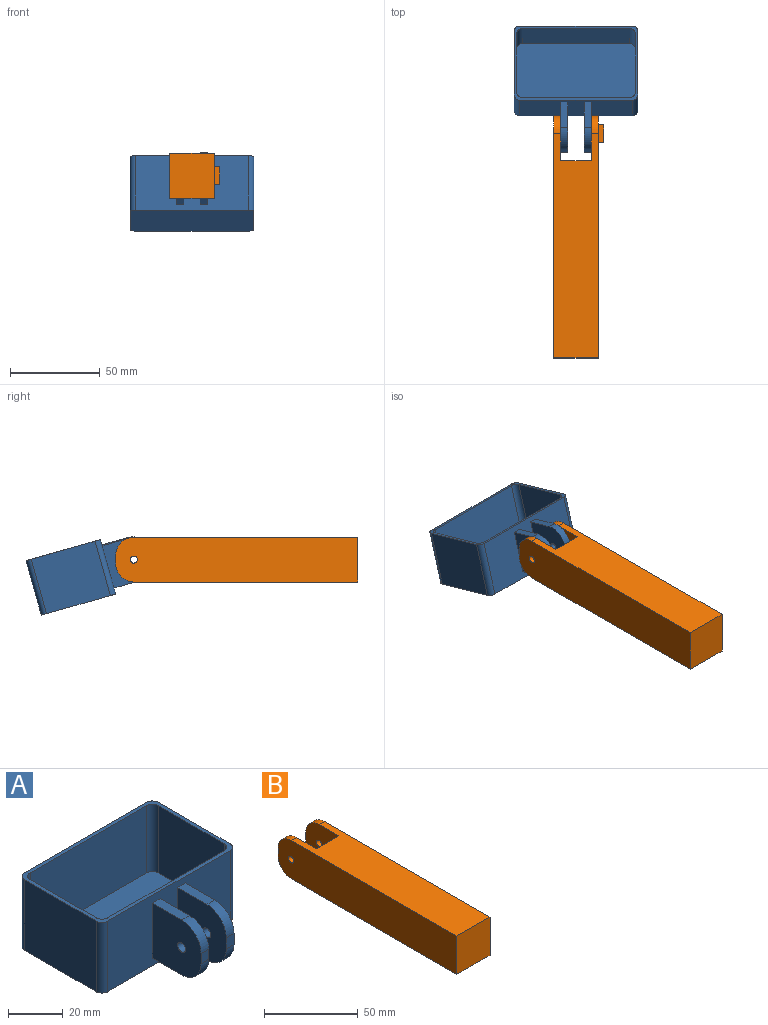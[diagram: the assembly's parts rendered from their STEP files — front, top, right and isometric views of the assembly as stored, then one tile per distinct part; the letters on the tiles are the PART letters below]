
ASSEMBLY  parts=2 mates=1
PART A: 35 faces, bbox 69x68x31.5 mm
  f0: plane 63x31.5mm, normal (0,-1,0), area 1786.5mm2, adj f4,f9,f15,f18,f19,f20,f21,f22
  f1: plane 37x31.5mm, normal (1,0,0), area 1165.5mm2, adj f4,f9,f15,f16
  f2: plane 63x31.5mm, normal (0,1,0), area 1984.5mm2, adj f4,f9,f16,f17
  f3: plane 37x31.5mm, normal (-1,0,0), area 1165.5mm2, adj f4,f9,f17,f18
  f4: plane 69x43mm, normal (0,0,-1), area 2959.3mm2, adj f0,f1,f2,f3,f15,f16,f17,f18
  f5: plane 60x30mm, normal (0,1,0), area 1800mm2, adj f9,f10,f11,f12
  f6: plane 34x30mm, normal (1,0,0), area 1020mm2, adj f9,f10,f11,f13
  f7: plane 60x30mm, normal (0,-1,0), area 1800mm2, adj f9,f10,f13,f14
  f8: plane 34x30mm, normal (-1,0,0), area 1020mm2, adj f9,f10,f12,f14
  f9: plane 69x43mm, normal (0,0,1), area 327mm2, adj f0,f1,f2,f3,f5,f6,f7,f8
  f10: plane 66x40mm, normal (0,0,1), area 2632.3mm2, adj f5,f6,f7,f8,f11,f12,f13,f14
  f11: cylinder r=3mm len=30mm, axis (0,0,1), area 141.4mm2, adj f5,f6,f9,f10
  f12: cylinder r=3mm len=30mm, axis (0,0,-1), area 141.4mm2, adj f5,f8,f9,f10
  f13: cylinder r=3mm len=30mm, axis (0,0,1), area 141.4mm2, adj f6,f7,f9,f10
  f14: cylinder r=3mm len=30mm, axis (0,0,-1), area 141.4mm2, adj f7,f8,f9,f10
  f15: cylinder r=3mm len=31.5mm, axis (0,0,1), area 148.4mm2, adj f0,f1,f4,f9
  f16: cylinder r=3mm len=31.5mm, axis (0,0,-1), area 148.4mm2, adj f1,f2,f4,f9
  f17: cylinder r=3mm len=31.5mm, axis (0,0,1), area 148.4mm2, adj f2,f3,f4,f9
  f18: cylinder r=3mm len=31.5mm, axis (0,0,-1), area 148.4mm2, adj f0,f3,f4,f9
  f19: plane 15x4mm, normal (0,0,1), area 60mm2, adj f0,f20,f22,f34
  f20: plane 25x24.5mm, normal (-1,0,0), area 557mm2, adj f0,f19,f21,f23,f30,f33,f34
  f21: plane 15x4mm, normal (0,0,-1), area 60mm2, adj f0,f20,f22,f33
  f22: plane 25x24.5mm, normal (1,0,0), area 557mm2, adj f0,f19,f21,f23,f30,f33,f34
  f23: plane 4.5x4mm, normal (0,-1,0), area 18mm2, adj f20,f22,f33,f34
  f24: plane 25x25mm, normal (1,0,0), area 569.5mm2, adj f0,f25,f27,f28,f29,f31,f32
  f25: plane 15x4mm, normal (0,0,1), area 60mm2, adj f0,f24,f26,f31
  f26: plane 25x25mm, normal (-1,0,0), area 569.5mm2, adj f0,f25,f27,f28,f29,f31,f32
  f27: plane 15x4mm, normal (0,0,-1), area 60mm2, adj f0,f24,f26,f32
  f28: plane 5x4mm, normal (0,-1,0), area 20mm2, adj f24,f26,f31,f32
  f29: cylinder r=2mm len=4mm, axis (-1,0,0), area 50.3mm2, adj f24,f26
  f30: cylinder r=2mm len=4mm, axis (-1,0,0), area 50.3mm2, adj f20,f22
  f31: cylinder r=10mm len=10mm, axis (1,0,0), area 62.8mm2, adj f24,f25,f26,f28
  f32: cylinder r=10mm len=10mm, axis (-1,0,0), area 62.8mm2, adj f24,f26,f27,f28
  f33: cylinder r=10mm len=10mm, axis (-1,0,0), area 62.8mm2, adj f20,f21,f22,f23
  f34: cylinder r=10mm len=10mm, axis (1,0,0), area 62.8mm2, adj f19,f20,f22,f23
PART B: 52 faces, bbox 28x135x25 mm
  f0: plane 25x17mm, normal (0,1,0), area 425mm2, adj f4,f5,f6,f8
  f1: plane 25x25mm, normal (0,-1,0), area 625mm2, adj f2,f3,f4,f5
  f2: plane 135x25mm, normal (1,0,0), area 3232.1mm2, adj f1,f4,f5,f7,f10,f11,f12,f13
  f3: plane 135x25mm, normal (-1,0,0), area 3319.5mm2, adj f1,f4,f5,f9,f22,f24,f25
  f4: plane 125x25mm, normal (0,0,-1), area 2870mm2, adj f0,f1,f2,f3,f6,f8,f24,f27
  f5: plane 125x25mm, normal (0,0,1), area 2870mm2, adj f0,f1,f2,f3,f6,f8,f25,f26
  f6: plane 25x25mm, normal (-1,0,0), area 569.5mm2, adj f0,f4,f5,f7,f23,f26,f27
  f7: plane 5x4mm, normal (0,1,0), area 20mm2, adj f2,f6,f26,f27
  f8: plane 25x25mm, normal (1,0,0), area 569.5mm2, adj f0,f4,f5,f9,f22,f24,f25
  f9: plane 5x4mm, normal (0,1,0), area 20mm2, adj f3,f8,f24,f25
  f10: plane 10x3mm, normal (0,0,-1), area 30mm2, adj f2,f11,f13,f14
  f11: plane 10x3mm, normal (0,1,0), area 30mm2, adj f2,f10,f12,f14
  f12: plane 10x3mm, normal (0,0,1), area 30mm2, adj f2,f11,f13,f14
  f13: plane 10x3mm, normal (0,-1,0), area 30mm2, adj f2,f10,f12,f14
  f14: plane 10x10mm, normal (1,0,0), area 57.6mm2, adj f10,f11,f12,f13,f15,f16,f17,f18
  f15: plane 3.5x3mm, normal (0,-0.5,0.87), area 12.1mm2, adj f14,f16,f20,f21
  f16: plane 4.04x3mm, normal (0,-1,0), area 12.1mm2, adj f14,f15,f17,f21
  f17: plane 3.5x3mm, normal (0,-0.5,-0.87), area 12.1mm2, adj f14,f16,f18,f21
  f18: plane 3.5x3mm, normal (0,0.5,-0.87), area 12.1mm2, adj f14,f17,f19,f21
  f19: plane 4.04x3mm, normal (0,1,0), area 12.1mm2, adj f14,f18,f20,f21
  f20: plane 3.5x3mm, normal (0,0.5,0.87), area 12.1mm2, adj f14,f15,f19,f21
  f21: plane 8.08x7mm, normal (1,0,0), area 29.9mm2, adj f15,f16,f17,f18,f19,f20,f23
  f22: cylinder r=2mm len=4mm, axis (1,0,0), area 50.3mm2, adj f3,f8
  f23: cylinder r=2mm len=4mm, axis (1,0,0), area 50.3mm2, adj f6,f21
  f24: cylinder r=10mm len=10mm, axis (1,0,0), area 62.8mm2, adj f3,f4,f8,f9
  f25: cylinder r=10mm len=10mm, axis (-1,0,0), area 62.8mm2, adj f3,f5,f8,f9
  f26: cylinder r=10mm len=10mm, axis (-1,0,0), area 62.8mm2, adj f2,f5,f6,f7
  f27: cylinder r=10mm len=10mm, axis (1,0,0), area 62.8mm2, adj f2,f4,f6,f7
  f28: plane 21x20mm, normal (0,0,-1), area 420mm2, adj f30,f31,f32,f33
  f29: plane 21x20mm, normal (0,0,1), area 420mm2, adj f30,f31,f32,f33
  f30: plane 21x20mm, normal (-1,0,0), area 420mm2, adj f28,f29,f31,f33
  f31: plane 21x21mm, normal (0,-1,0), area 441mm2, adj f28,f29,f30,f32
  f32: plane 21x20mm, normal (1,0,0), area 420mm2, adj f28,f29,f31,f33
  f33: plane 21x21mm, normal (0,1,0), area 441mm2, adj f28,f29,f30,f32
  f34: plane 21x20mm, normal (0,0,1), area 420mm2, adj f35,f36,f37,f38
  f35: plane 21x21mm, normal (0,1,0), area 441mm2, adj f34,f36,f38,f39
  f36: plane 21x20mm, normal (-1,0,0), area 420mm2, adj f34,f35,f37,f39
  f37: plane 21x21mm, normal (0,-1,0), area 441mm2, adj f34,f36,f38,f39
  f38: plane 21x20mm, normal (1,0,0), area 420mm2, adj f34,f35,f37,f39
  f39: plane 21x20mm, normal (0,0,-1), area 420mm2, adj f35,f36,f37,f38
  f40: plane 30x21mm, normal (0,0,1), area 630mm2, adj f41,f42,f43,f44
  f41: plane 21x21mm, normal (0,1,0), area 441mm2, adj f40,f42,f44,f45
  f42: plane 30x21mm, normal (-1,0,0), area 630mm2, adj f40,f41,f43,f45
  f43: plane 21x21mm, normal (0,-1,0), area 441mm2, adj f40,f42,f44,f45
  f44: plane 30x21mm, normal (1,0,0), area 630mm2, adj f40,f41,f43,f45
  f45: plane 30x21mm, normal (0,0,-1), area 630mm2, adj f41,f42,f43,f44
  f46: plane 30x21mm, normal (0,0,-1), area 630mm2, adj f48,f49,f50,f51
  f47: plane 30x21mm, normal (0,0,1), area 630mm2, adj f48,f49,f50,f51
  f48: plane 30x21mm, normal (-1,0,0), area 630mm2, adj f46,f47,f49,f51
  f49: plane 21x21mm, normal (0,-1,0), area 441mm2, adj f46,f47,f48,f50
  f50: plane 30x21mm, normal (1,0,0), area 630mm2, adj f46,f47,f49,f51
  f51: plane 21x21mm, normal (0,1,0), area 441mm2, adj f46,f47,f48,f50
PLACE A rot(axis=(-1,0,0),15.8deg) t=(18.53,82.09,-35.53)mm
PLACE B t=(-31.47,-28.38,-20.24)mm fixed
MATE revolute A.f29 <-> B.f22  axis (1,0,0) through (-22.97,41.62,-7.74)mm
